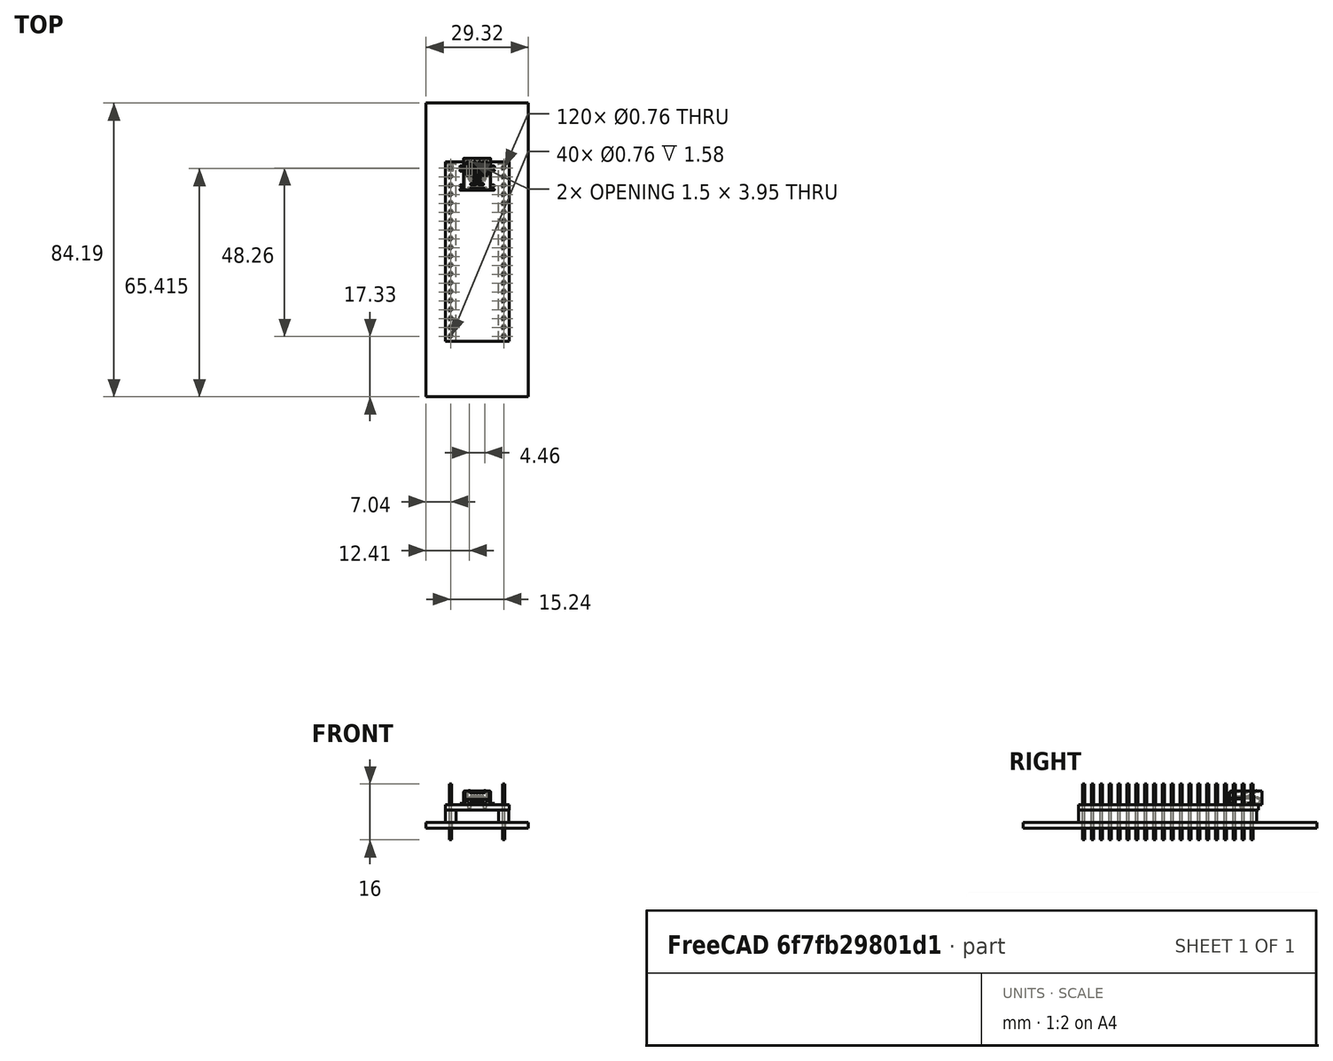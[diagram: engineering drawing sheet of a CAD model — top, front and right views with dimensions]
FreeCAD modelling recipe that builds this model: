
FCSTD DOCUMENT  (FreeCAD 0.18R16146 (Git))
Label: maplemini
License: All rights reserved
LicenseURL: http://en.wikipedia.org/wiki/All_rights_reserved
objects: Part::Box×42, Part::MultiFuse×10, Part::FeaturePython×7, Part::Feature×4, App::DocumentObjectGroup×1
note: 63 computed .brp shape members not serialized (recipe doc carries the construction recipe); baked Part::Feature solids carry a one-line shape summary decoded from their .brp

FEATURE [Part::FeaturePython] FCrtYd_lines  label="FCrtYd"  # a2plus imported part (geometry in sourceFile) (typed FeaturePython)
  fixedPosition = true
FEATURE [Part::FeaturePython] FFab_lines  label="FFab"  # a2plus imported part (geometry in sourceFile) (typed FeaturePython)
  fixedPosition = true
FEATURE [Part::FeaturePython] Filk_lines  label="FrontSilk"  # a2plus imported part (geometry in sourceFile) (typed FeaturePython)
  fixedPosition = true
FEATURE [Part::FeaturePython] TopPads  # a2plus imported part (geometry in sourceFile) (typed FeaturePython)
  fixedPosition = true
FEATURE [Part::FeaturePython] BotPads  # a2plus imported part (geometry in sourceFile) (typed FeaturePython)
  fixedPosition = true
FEATURE [Part::FeaturePython] THPs  label="PTHs"  # a2plus imported part (geometry in sourceFile) (typed FeaturePython)
  fixedPosition = true
FEATURE [Part::FeaturePython] newPCB  label="Pcb"  # a2plus imported part (geometry in sourceFile) (typed FeaturePython)
  fixedPosition = true
FEATURE [App::DocumentObjectGroup] Maple_Mini_fp
  Group = -> [FCrtYd_lines,FFab_lines,Filk_lines,TopPads,BotPads,THPs,newPCB]
FEATURE [Part::Box] Box001  label="Würfel001"
  AttacherType = Attacher::AttachEngine3D
  Height = 3.5
  Length = 3
  Placement = pos=(-1.5,-49.7,0) rot=(0,0,1;0rad)
  Width = 51
FEATURE [Part::Box] Box002  label="Würfel002"
  AttacherType = Attacher::AttachEngine3D
  Height = 3.5
  Length = 3
  Placement = pos=(13.7,-49.7,0) rot=(0,0,1;0rad)
  Width = 51
FEATURE [Part::Box] Box003  label="Würfel003"
  AttacherType = Attacher::AttachEngine3D
  Height = 11
  Length = 0.6
  Placement = pos=(-0.3,-0.3,0) rot=(0,0,1;0rad)
  Width = 0.6
FEATURE [Part::Box] Box004  label="Würfel004"
  AttacherType = Attacher::AttachEngine3D
  Height = 11
  Length = 0.6
  Placement = pos=(-0.3,-2.84,0) rot=(0,0,1;0rad)
  Width = 0.6
FEATURE [Part::Box] Box005  label="Würfel005"
  AttacherType = Attacher::AttachEngine3D
  Height = 11
  Length = 0.6
  Placement = pos=(-0.3,-5.38,0) rot=(0,0,1;0rad)
  Width = 0.6
FEATURE [Part::Box] Box006  label="Würfel006"
  AttacherType = Attacher::AttachEngine3D
  Height = 11
  Length = 0.6
  Placement = pos=(-0.3,-7.92,0) rot=(0,0,1;0rad)
  Width = 0.6
FEATURE [Part::Box] Box007  label="Würfel007"
  AttacherType = Attacher::AttachEngine3D
  Height = 11
  Length = 0.6
  Placement = pos=(-0.3,-10.46,0) rot=(0,0,1;0rad)
  Width = 0.6
FEATURE [Part::MultiFuse] Fusion
  Shapes = -> [Box003,Box004,Box005,Box006,Box007]
FEATURE [Part::Box] Box008  label="Würfel008"
  AttacherType = Attacher::AttachEngine3D
  Height = 11
  Length = 0.6
  Placement = pos=(-0.3,-2.84,0) rot=(0,0,1;0rad)
  Width = 0.6
FEATURE [Part::Box] Box009  label="Würfel009"
  AttacherType = Attacher::AttachEngine3D
  Height = 11
  Length = 0.6
  Placement = pos=(-0.3,-5.38,0) rot=(0,0,1;0rad)
  Width = 0.6
FEATURE [Part::Box] Box010  label="Würfel010"
  AttacherType = Attacher::AttachEngine3D
  Height = 11
  Length = 0.6
  Placement = pos=(-0.3,-7.92,0) rot=(0,0,1;0rad)
  Width = 0.6
FEATURE [Part::Box] Box011  label="Würfel011"
  AttacherType = Attacher::AttachEngine3D
  Height = 11
  Length = 0.6
  Placement = pos=(-0.3,-0.3,0) rot=(0,0,1;0rad)
  Width = 0.6
FEATURE [Part::Box] Box012  label="Würfel012"
  AttacherType = Attacher::AttachEngine3D
  Height = 11
  Length = 0.6
  Placement = pos=(-0.3,-10.46,0) rot=(0,0,1;0rad)
  Width = 0.6
FEATURE [Part::MultiFuse] Fusion001
  Placement = pos=(0,-12.7,0) rot=(0,0,1;0rad)
  Shapes = -> [Box011,Box008,Box009,Box010,Box012]
FEATURE [Part::Box] Box013  label="Würfel013"
  AttacherType = Attacher::AttachEngine3D
  Height = 11
  Length = 0.6
  Placement = pos=(-0.3,-0.3,0) rot=(0,0,1;0rad)
  Width = 0.6
FEATURE [Part::Box] Box014  label="Würfel014"
  AttacherType = Attacher::AttachEngine3D
  Height = 11
  Length = 0.6
  Placement = pos=(-0.3,-2.84,0) rot=(0,0,1;0rad)
  Width = 0.6
FEATURE [Part::Box] Box015  label="Würfel015"
  AttacherType = Attacher::AttachEngine3D
  Height = 11
  Length = 0.6
  Placement = pos=(-0.3,-5.38,0) rot=(0,0,1;0rad)
  Width = 0.6
FEATURE [Part::Box] Box016  label="Würfel016"
  AttacherType = Attacher::AttachEngine3D
  Height = 11
  Length = 0.6
  Placement = pos=(-0.3,-7.92,0) rot=(0,0,1;0rad)
  Width = 0.6
FEATURE [Part::Box] Box017  label="Würfel017"
  AttacherType = Attacher::AttachEngine3D
  Height = 11
  Length = 0.6
  Placement = pos=(-0.3,-10.46,0) rot=(0,0,1;0rad)
  Width = 0.6
FEATURE [Part::MultiFuse] Fusion002
  Placement = pos=(0,-25.4,0) rot=(0,0,1;0rad)
  Shapes = -> [Box013,Box014,Box015,Box016,Box017]
FEATURE [Part::Box] Box018  label="Würfel018"
  AttacherType = Attacher::AttachEngine3D
  Height = 11
  Length = 0.6
  Placement = pos=(-0.3,-0.3,0) rot=(0,0,1;0rad)
  Width = 0.6
FEATURE [Part::Box] Box019  label="Würfel019"
  AttacherType = Attacher::AttachEngine3D
  Height = 11
  Length = 0.6
  Placement = pos=(-0.3,-2.84,0) rot=(0,0,1;0rad)
  Width = 0.6
FEATURE [Part::Box] Box020  label="Würfel020"
  AttacherType = Attacher::AttachEngine3D
  Height = 11
  Length = 0.6
  Placement = pos=(-0.3,-5.38,0) rot=(0,0,1;0rad)
  Width = 0.6
FEATURE [Part::Box] Box021  label="Würfel021"
  AttacherType = Attacher::AttachEngine3D
  Height = 11
  Length = 0.6
  Placement = pos=(-0.3,-7.92,0) rot=(0,0,1;0rad)
  Width = 0.6
FEATURE [Part::Box] Box022  label="Würfel022"
  AttacherType = Attacher::AttachEngine3D
  Height = 11
  Length = 0.6
  Placement = pos=(-0.3,-10.46,0) rot=(0,0,1;0rad)
  Width = 0.6
FEATURE [Part::MultiFuse] Fusion003
  Placement = pos=(0,-38.1,0) rot=(0,0,1;0rad)
  Shapes = -> [Box018,Box019,Box020,Box021,Box022]
FEATURE [Part::MultiFuse] Fusion004
  Shapes = -> [Fusion,Fusion001,Fusion003,Fusion002]
FEATURE [Part::Box] Box023  label="Würfel023"
  AttacherType = Attacher::AttachEngine3D
  Height = 11
  Length = 0.6
  Placement = pos=(-0.3,-0.3,0) rot=(0,0,1;0rad)
  Width = 0.6
FEATURE [Part::Box] Box024  label="Würfel024"
  AttacherType = Attacher::AttachEngine3D
  Height = 11
  Length = 0.6
  Placement = pos=(-0.3,-2.84,0) rot=(0,0,1;0rad)
  Width = 0.6
FEATURE [Part::Box] Box025  label="Würfel025"
  AttacherType = Attacher::AttachEngine3D
  Height = 11
  Length = 0.6
  Placement = pos=(-0.3,-7.92,0) rot=(0,0,1;0rad)
  Width = 0.6
FEATURE [Part::Box] Box026  label="Würfel026"
  AttacherType = Attacher::AttachEngine3D
  Height = 11
  Length = 0.6
  Placement = pos=(-0.3,-10.46,0) rot=(0,0,1;0rad)
  Width = 0.6
FEATURE [Part::Box] Box027  label="Würfel027"
  AttacherType = Attacher::AttachEngine3D
  Height = 11
  Length = 0.6
  Placement = pos=(-0.3,-0.3,0) rot=(0,0,1;0rad)
  Width = 0.6
FEATURE [Part::Box] Box028  label="Würfel028"
  AttacherType = Attacher::AttachEngine3D
  Height = 11
  Length = 0.6
  Placement = pos=(-0.3,-10.46,0) rot=(0,0,1;0rad)
  Width = 0.6
FEATURE [Part::Box] Box029  label="Würfel029"
  AttacherType = Attacher::AttachEngine3D
  Height = 11
  Length = 0.6
  Placement = pos=(-0.3,-5.38,0) rot=(0,0,1;0rad)
  Width = 0.6
FEATURE [Part::Box] Box030  label="Würfel030"
  AttacherType = Attacher::AttachEngine3D
  Height = 11
  Length = 0.6
  Placement = pos=(-0.3,-5.38,0) rot=(0,0,1;0rad)
  Width = 0.6
FEATURE [Part::Box] Box031  label="Würfel031"
  AttacherType = Attacher::AttachEngine3D
  Height = 11
  Length = 0.6
  Placement = pos=(-0.3,-2.84,0) rot=(0,0,1;0rad)
  Width = 0.6
FEATURE [Part::Box] Box032  label="Würfel032"
  AttacherType = Attacher::AttachEngine3D
  Height = 11
  Length = 0.6
  Placement = pos=(-0.3,-5.38,0) rot=(0,0,1;0rad)
  Width = 0.6
FEATURE [Part::Box] Box033  label="Würfel033"
  AttacherType = Attacher::AttachEngine3D
  Height = 11
  Length = 0.6
  Placement = pos=(-0.3,-7.92,0) rot=(0,0,1;0rad)
  Width = 0.6
FEATURE [Part::Box] Box034  label="Würfel034"
  AttacherType = Attacher::AttachEngine3D
  Height = 11
  Length = 0.6
  Placement = pos=(-0.3,-7.92,0) rot=(0,0,1;0rad)
  Width = 0.6
FEATURE [Part::Box] Box035  label="Würfel035"
  AttacherType = Attacher::AttachEngine3D
  Height = 11
  Length = 0.6
  Placement = pos=(-0.3,-2.84,0) rot=(0,0,1;0rad)
  Width = 0.6
FEATURE [Part::Box] Box036  label="Würfel036"
  AttacherType = Attacher::AttachEngine3D
  Height = 11
  Length = 0.6
  Placement = pos=(-0.3,-10.46,0) rot=(0,0,1;0rad)
  Width = 0.6
FEATURE [Part::MultiFuse] Fusion005
  Placement = pos=(0,-12.7,0) rot=(0,0,1;0rad)
  Shapes = -> [Box023,Box024,Box029,Box034,Box036]
FEATURE [Part::Box] Box037  label="Würfel037"
  AttacherType = Attacher::AttachEngine3D
  Height = 11
  Length = 0.6
  Placement = pos=(-0.3,-2.84,0) rot=(0,0,1;0rad)
  Width = 0.6
FEATURE [Part::Box] Box038  label="Würfel038"
  AttacherType = Attacher::AttachEngine3D
  Height = 11
  Length = 0.6
  Placement = pos=(-0.3,-5.38,0) rot=(0,0,1;0rad)
  Width = 0.6
FEATURE [Part::Box] Box039  label="Würfel039"
  AttacherType = Attacher::AttachEngine3D
  Height = 11
  Length = 0.6
  Placement = pos=(-0.3,-7.92,0) rot=(0,0,1;0rad)
  Width = 0.6
FEATURE [Part::Box] Box040  label="Würfel040"
  AttacherType = Attacher::AttachEngine3D
  Height = 11
  Length = 0.6
  Placement = pos=(-0.3,-0.3,0) rot=(0,0,1;0rad)
  Width = 0.6
FEATURE [Part::MultiFuse] Fusion008
  Placement = pos=(0,-38.1,0) rot=(0,0,1;0rad)
  Shapes = -> [Box040,Box035,Box032,Box033,Box028]
FEATURE [Part::MultiFuse] Fusion009
  Placement = pos=(0,-25.4,0) rot=(0,0,1;0rad)
  Shapes = -> [Box027,Box031,Box030,Box025,Box026]
FEATURE [Part::Box] Box041  label="Würfel041"
  AttacherType = Attacher::AttachEngine3D
  Height = 11
  Length = 0.6
  Placement = pos=(-0.3,-0.3,0) rot=(0,0,1;0rad)
  Width = 0.6
FEATURE [Part::Box] Box042  label="Würfel042"
  AttacherType = Attacher::AttachEngine3D
  Height = 11
  Length = 0.6
  Placement = pos=(-0.3,-10.46,0) rot=(0,0,1;0rad)
  Width = 0.6
FEATURE [Part::MultiFuse] Fusion006
  Shapes = -> [Box041,Box037,Box038,Box039,Box042]
FEATURE [Part::MultiFuse] Fusion007
  Placement = pos=(15.25,0,0) rot=(0,0,1;0rad)
  Shapes = -> [Fusion006,Fusion005,Fusion008,Fusion009]
FEATURE [Part::Feature] Shape001  label="pcb"
  shape: bbox 18.3 x 51.5 x 1.6 mm, 6 faces (baked)
FEATURE [Part::Feature] Shape002  label="header"
  shape: bbox 18.2 x 51 x 3.5 mm, 12 faces, 2 solids (baked)
FEATURE [Part::Feature] Shape003  label="pins"
  shape: bbox 15.85 x 48.86 x 11 mm, 240 faces, 40 solids (baked)
FEATURE [Part::Feature] Shape  label="usb"
  shape: bbox 9.9 x 9.2 x 4.997 mm, 472 faces (baked)
